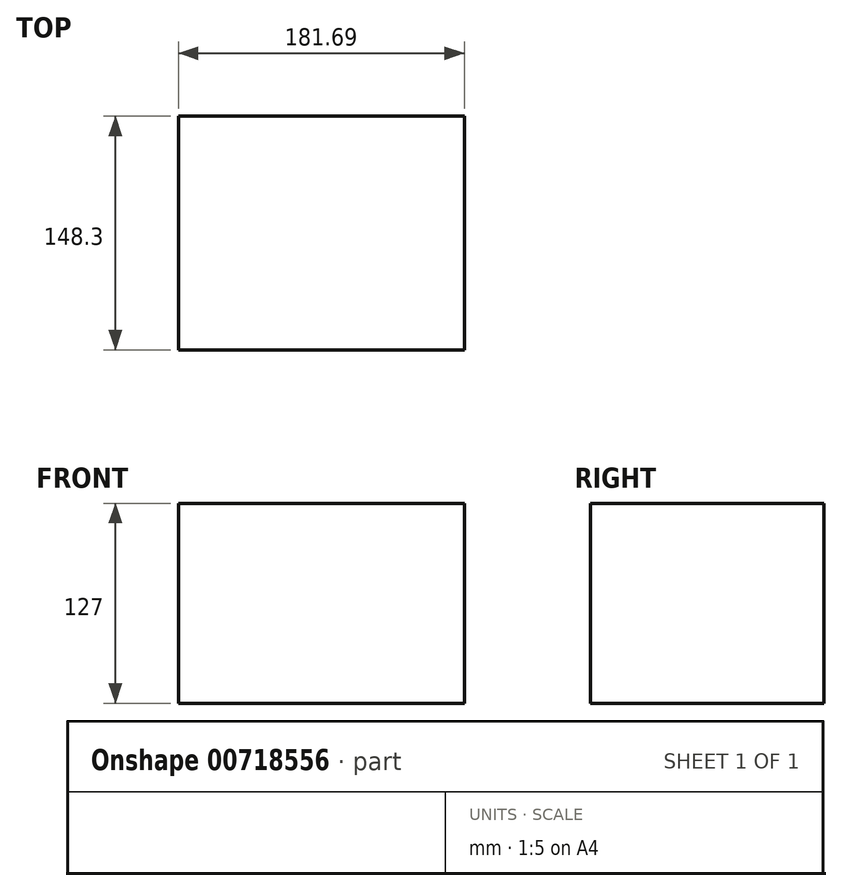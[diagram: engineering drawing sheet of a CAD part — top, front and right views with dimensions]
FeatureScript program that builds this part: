
annotation { "Feature Type Name" : "Feature", "Feature Type Description" : "" }
export const myFeature = defineFeature(function(context is Context, id is Id, definition is map)
    precondition{}
    {
        {
            var Q0;
            Q0=qCreatedBy(makeId("Top.planeOp"),FACE);
            var sketch = newSketch(context, id + "F0", { "sketchPlane" : qUnion([Q0])});
            skLineSegment(sketch, "E0.bottom", {"start": v(-153.6, 35.92) * mm, "end": v(28.1, 35.92) * mm});
            skLineSegment(sketch, "E0.top", {"start": v(-153.6, -112.38) * mm, "end": v(28.1, -112.38) * mm});
            skLineSegment(sketch, "E0.left", {"start": v(-153.6, 35.92) * mm, "end": v(-153.6, -112.38) * mm});
            skLineSegment(sketch, "E0.right", {"start": v(28.1, 35.92) * mm, "end": v(28.1, -112.38) * mm});
            skSolve(sketch);
        }
        {
            var Q0;
            Q0 = qSketchRegion(id + "F0", true);
            extrude(context, id + "F1", {"entities" : qUnion([Q0]), "depth" : 127 * mm, "offsetDistance" : 25.4 * mm});
        }
        {
            var Q0;
            Q0=makeQuery(id+"F1.opExtrude","SWEPT_FACE",FACE,{"disambiguationData":[OSD([sQuery(id+"F0.wireOp",EDGE,"E0.top")])]});
            var sketch = newSketch(context, id + "F2", { "sketchPlane" : qUnion([Q0])});
            skFitSpline(sketch, "E1", {"points": [v(-81.43, 127) * mm, v(-43.36, 76.2) * mm, v(-58.73, 22.35) * mm, v(28.1, 54.57) * mm, v(-36.69, 127) * mm], "startDerivative": vector(265.65, -193.42) * mm, "endDerivative": vector(-414.37, 264.39) * mm});
            skSolve(sketch);
        }
    });
